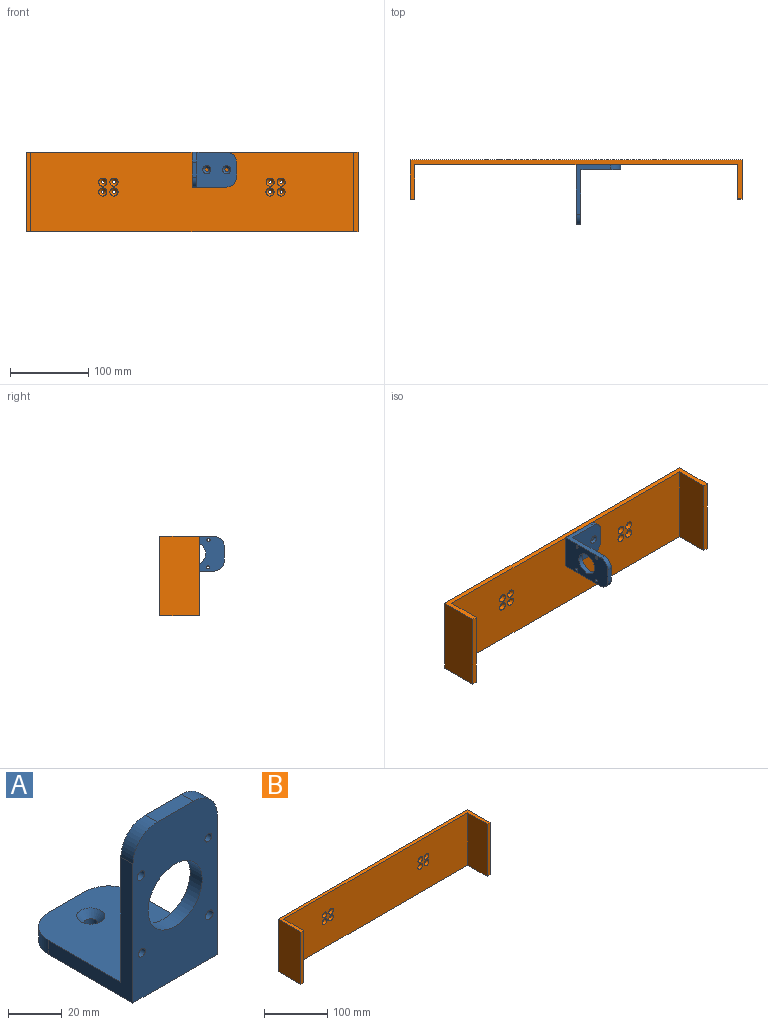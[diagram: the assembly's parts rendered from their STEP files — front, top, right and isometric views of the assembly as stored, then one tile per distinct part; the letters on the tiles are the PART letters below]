
ASSEMBLY  parts=2 mates=1
PART A: 21 faces, bbox 44.5x57.2x76.2 mm
  f0: plane 69.85x44.45mm, normal (0,1,0), area 2352.1mm2, adj f2,f3,f4,f5,f7,f8,f9,f10
  f1: plane 57.15x44.45mm, normal (0,0,-1), area 2430.1mm2, adj f2,f5,f6,f11,f13,f14,f17,f19
  f2: plane 63.5x44.45mm, normal (1,0,0), area 645.2mm2, adj f0,f1,f6,f12,f13,f15
  f3: plane 19.05x6.35mm, normal (0,0,1), area 121mm2, adj f0,f6,f15,f16
  f4: cylinder r=14.25mm len=28.5mm, axis (0,1,0), area 568.5mm2, adj f0,f6
  f5: plane 63.5x44.45mm, normal (-1,0,0), area 645.2mm2, adj f0,f1,f6,f12,f14,f16
  f6: plane 76.2x44.45mm, normal (0,-1,0), area 2634.4mm2, adj f1,f2,f3,f4,f5,f7,f8,f9
  f7: cylinder r=2.02mm len=6.35mm, axis (0,1,0), area 80.6mm2, adj f0,f6
  f8: cylinder r=1.78mm len=6.35mm, axis (0,1,0), area 71.1mm2, adj f0,f6
  f9: cylinder r=2.02mm len=6.35mm, axis (0,1,0), area 80.6mm2, adj f0,f6
  f10: cylinder r=1.78mm len=6.35mm, axis (0,1,0), area 71.1mm2, adj f0,f6
  f11: plane 19.05x6.35mm, normal (0,1,0), area 121mm2, adj f1,f12,f13,f14
  f12: plane 50.8x44.45mm, normal (0,0,1), area 2017.6mm2, adj f0,f2,f5,f11,f13,f14,f18,f20
  f13: cylinder r=12.7mm len=12.7mm, axis (0,0,-1), area 126.7mm2, adj f1,f2,f11,f12
  f14: cylinder r=12.7mm len=12.7mm, axis (0,0,1), area 126.7mm2, adj f1,f5,f11,f12
  f15: cylinder r=12.7mm len=12.7mm, axis (0,1,0), area 126.7mm2, adj f0,f2,f3,f6
  f16: cylinder r=12.7mm len=12.7mm, axis (0,-1,0), area 126.7mm2, adj f0,f3,f5,f6
  f17: cylinder r=2.55mm len=5.11mm, axis (0,0,1), area 52.6mm2, adj f1,f18
  f18: cone r=2.55mm half-angle=41deg, axis (0,0,1), area 99.3mm2, adj f12,f17
  f19: cylinder r=2.55mm len=5.11mm, axis (0,0,1), area 52.6mm2, adj f1,f20
  f20: cone r=2.55mm half-angle=41deg, axis (0,0,1), area 99.3mm2, adj f12,f19
PART B: 26 faces, bbox 425.5x50.8x101.6 mm
  f0: plane 101.6x50.8mm, normal (-1,0,0), area 5161.3mm2, adj f1,f4,f24,f25
  f1: plane 101.6x6.35mm, normal (0,-1,0), area 645.2mm2, adj f0,f5,f24,f25
  f2: plane 101.6x6.35mm, normal (0,-1,0), area 645.2mm2, adj f3,f7,f24,f25
  f3: plane 101.6x50.14mm, normal (1,0,0), area 5093.9mm2, adj f2,f4,f24,f25
  f4: plane 425.45x101.6mm, normal (0,1,0), area 43135.1mm2, adj f0,f3,f8,f10,f12,f14,f16,f18
  f5: plane 101.6x44.45mm, normal (1,0,0), area 4516.1mm2, adj f1,f6,f24,f25
  f6: plane 412.75x101.6mm, normal (0,-1,0), area 41250.7mm2, adj f5,f7,f9,f11,f13,f15,f17,f19
  f7: plane 101.6x43.79mm, normal (-1,0,0), area 4448.7mm2, adj f2,f6,f24,f25
  f8: cylinder r=1.9mm len=3.8mm, axis (0,-1,0), area 30.2mm2, adj f4,f9
  f9: cone r=1.9mm half-angle=41deg, axis (0,-1,0), area 113.2mm2, adj f6,f8
  f10: cylinder r=1.9mm len=3.8mm, axis (0,-1,0), area 30.2mm2, adj f4,f11
  f11: cone r=1.9mm half-angle=41deg, axis (0,-1,0), area 113.2mm2, adj f6,f10
  f12: cylinder r=1.9mm len=3.8mm, axis (0,-1,0), area 30.2mm2, adj f4,f13
  f13: cone r=1.9mm half-angle=41deg, axis (0,-1,0), area 113.2mm2, adj f6,f12
  f14: cylinder r=1.9mm len=3.8mm, axis (0,-1,0), area 30.2mm2, adj f4,f15
  f15: cone r=1.9mm half-angle=41deg, axis (0,-1,0), area 113.2mm2, adj f6,f14
  f16: cylinder r=1.9mm len=3.8mm, axis (0,-1,0), area 30.2mm2, adj f4,f17
  f17: cone r=1.9mm half-angle=41deg, axis (0,-1,0), area 113.2mm2, adj f6,f16
  f18: cylinder r=1.9mm len=3.8mm, axis (0,-1,0), area 30.2mm2, adj f4,f19
  f19: cone r=1.9mm half-angle=41deg, axis (0,-1,0), area 113.2mm2, adj f6,f18
  f20: cylinder r=1.9mm len=3.8mm, axis (0,-1,0), area 30.2mm2, adj f4,f21
  f21: cone r=1.9mm half-angle=41deg, axis (0,-1,0), area 113.2mm2, adj f6,f20
  f22: cylinder r=1.9mm len=3.8mm, axis (0,-1,0), area 30.2mm2, adj f4,f23
  f23: cone r=1.9mm half-angle=41deg, axis (0,-1,0), area 113.2mm2, adj f6,f22
  f24: plane 425.45x50.8mm, normal (0,0,1), area 3261.9mm2, adj f0,f1,f2,f3,f4,f5,f6,f7
  f25: plane 425.45x50.8mm, normal (0,0,-1), area 3261.9mm2, adj f0,f1,f2,f3,f4,f5,f6,f7
PLACE A rot(axis=(0.58,0.58,-0.58),120deg) t=(-148.73,-24.59,273.43)mm
PLACE B t=(-342.51,-18.24,155.96)mm
MATE fastened B.f6 <-> A.f1  axis (0,-1,0) through (-151.91,13.51,295.66)mm
